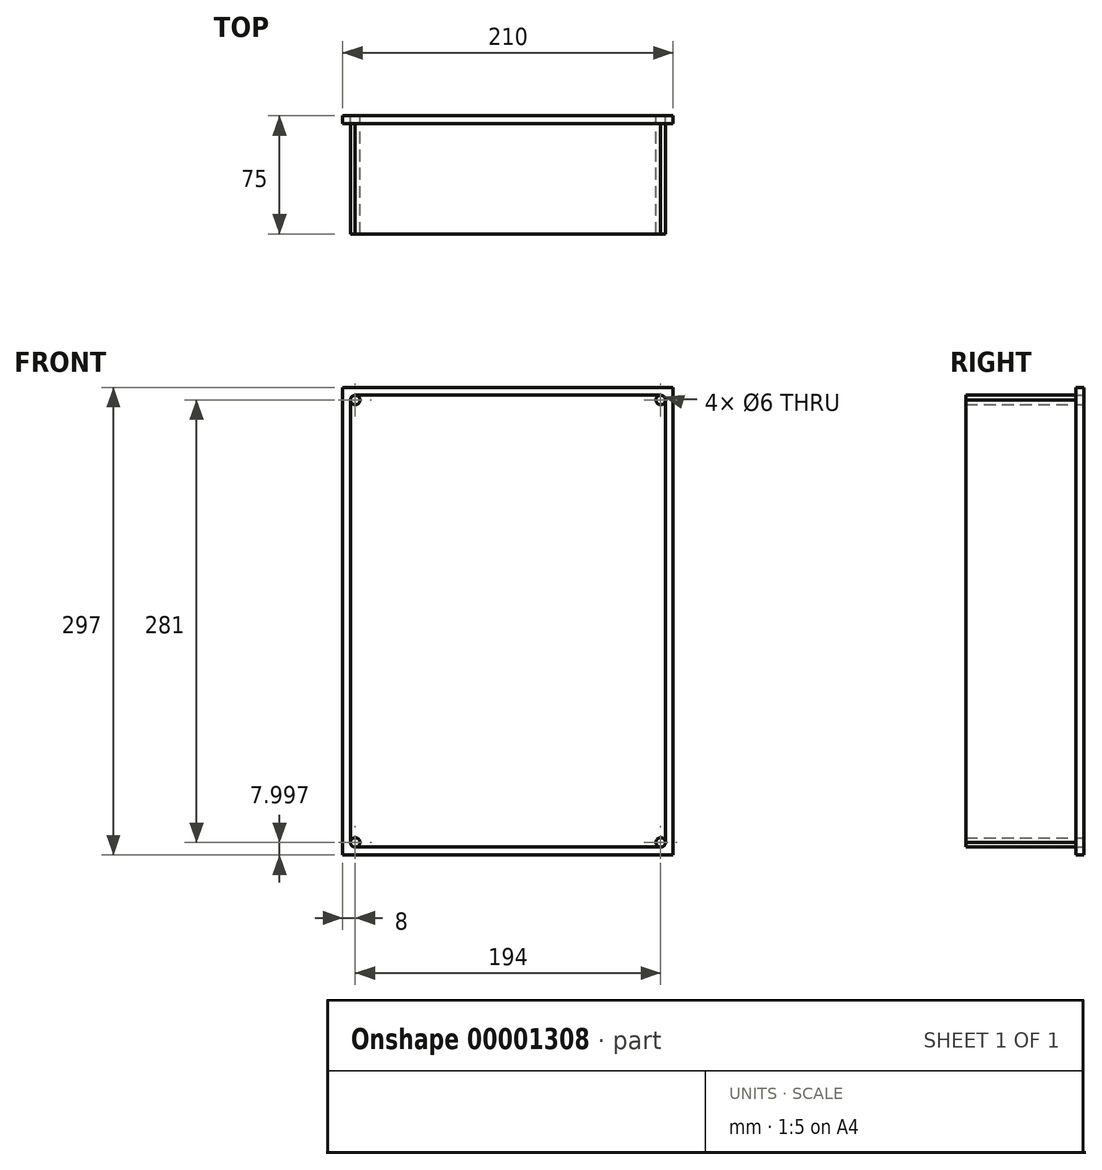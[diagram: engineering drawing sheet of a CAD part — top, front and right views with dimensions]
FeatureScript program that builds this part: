
annotation { "Feature Type Name" : "Feature", "Feature Type Description" : "" }
export const myFeature = defineFeature(function(context is Context, id is Id, definition is map)
    precondition{}
    {
        {
            var Q0;
            Q0=qCreatedBy(makeId("Front.planeOp"),FACE);
            var sketch = newSketch(context, id + "F0", { "sketchPlane" : qUnion([Q0])});
            skLineSegment(sketch, "E0.bottom", {"start": v(0, 297.27) * mm, "end": v(-210, 297.27) * mm});
            skLineSegment(sketch, "E0.top", {"start": v(0, 594.27) * mm, "end": v(-210, 594.27) * mm});
            skLineSegment(sketch, "E0.left", {"start": v(0, 297.27) * mm, "end": v(0, 594.27) * mm});
            skLineSegment(sketch, "E0.right", {"start": v(-210, 297.27) * mm, "end": v(-210, 594.27) * mm});
            skCircle(sketch, "E1", {"center": v(-8, 305.27) * mm, "radius": 3 * mm});
            skCircle(sketch, "E2", {"center": v(-202, 305.27) * mm, "radius": 3 * mm});
            skCircle(sketch, "E3", {"center": v(-8, 586.27) * mm, "radius": 3 * mm});
            skCircle(sketch, "E4", {"center": v(-202, 586.27) * mm, "radius": 3 * mm});
            skSolve(sketch);
        }
        {
            var Q0;
            Q0 = qSketchRegion(id + "F0", true);
            extrude(context, id + "F1", {"entities" : qUnion([Q0]), "depth" : 5 * mm, "offsetDistance" : 25 * mm});
        }
        {
            var Q0;
            Q0=makeQuery(id+"F0.imprint","IMPRINT",FACE,{"disambiguationData":[TD([[makeQuery(id+"F0.imprint","IMPRINT",EDGE,{"derivedFrom":sQuery(id+"F0.wireOp",EDGE,"E0.bottom")}),-1.0]])]});
            extrude(context, id + "F2", {"entities" : qUnion([Q0]), "depth" : 5 * mm, "offsetDistance" : 25 * mm});
        }
        {
            var Q0;
            Q0=makeQuery(id+"F2.opExtrude","SWEPT_EDGE",EDGE,{"disambiguationData":[OSD([sQuery(id+"F0.wireOp",EDGE,"E0.top"),sQuery(id+"F0.wireOp",EDGE,"E0.left")])]});
            var Q1;
            Q1=makeQuery(id+"F2.opExtrude","SWEPT_EDGE",EDGE,{"disambiguationData":[OSD([sQuery(id+"F0.wireOp",EDGE,"E0.bottom"),sQuery(id+"F0.wireOp",EDGE,"E0.left")])]});
            var Q2;
            Q2=makeQuery(id+"F2.opExtrude","SWEPT_EDGE",EDGE,{"disambiguationData":[OSD([sQuery(id+"F0.wireOp",EDGE,"E0.bottom"),sQuery(id+"F0.wireOp",EDGE,"E0.right")])]});
            var Q3;
            Q3=makeQuery(id+"F2.opExtrude","SWEPT_EDGE",EDGE,{"disambiguationData":[OSD([sQuery(id+"F0.wireOp",EDGE,"E0.top"),sQuery(id+"F0.wireOp",EDGE,"E0.right")])]});
            fillet(context, id + "F3", {"entities" : qUnion([Q0, Q1, Q2, Q3]), "radius" : 5 * mm, "tangentPropagation" : true, "allowEdgeOverflow" : false});
        }
        {
            var Q0;
            Q0=makeQuery(id+"F2.opExtrude","CAP_FACE",FACE,{"disambiguationData":[OSD([sQuery(id+"F0.wireOp",EDGE,"E0.bottom"),sQuery(id+"F0.wireOp",EDGE,"E0.top"),sQuery(id+"F0.wireOp",EDGE,"E0.left"),sQuery(id+"F0.wireOp",EDGE,"E0.right"),sQuery(id+"F0.wireOp",EDGE,"E1"),sQuery(id+"F0.wireOp",EDGE,"E2"),sQuery(id+"F0.wireOp",EDGE,"E3"),sQuery(id+"F0.wireOp",EDGE,"E4")])],"isStart":false});
            var sketch = newSketch(context, id + "F4", { "sketchPlane" : qUnion([Q0])});
            skLineSegment(sketch, "E5.bottom", {"start": v(-205, 589.27) * mm, "end": v(-5, 589.27) * mm});
            skLineSegment(sketch, "E5.top", {"start": v(-205, 302.27) * mm, "end": v(-8, 302.27) * mm});
            skLineSegment(sketch, "E5.left", {"start": v(-205, 589.27) * mm, "end": v(-205, 302.27) * mm});
            skLineSegment(sketch, "E5.right", {"start": v(-5, 589.27) * mm, "end": v(-5, 302.27) * mm});
            skSolve(sketch);
        }
        {
            var Q0;
            Q0 = qSketchRegion(id + "F4", true);
            var Q1;
            {var subQ10=makeQuery(id+"F2.opExtrude","CAP_EDGE",EDGE,{"disambiguationData":[OSD([sQuery(id+"F0.wireOp",EDGE,"E4")])],"isStart":false});var subQ13=sQuery(id+"F4.wireOp",EDGE,"E5.bottom");var subQ14=makeQuery(id+"F4.imprint","INTERSECT",VERTEX,{"derivedFrom":[subQ10,subQ13]});Q1=makeQuery(id+"F4.imprint","IMPRINT",FACE,{"disambiguationData":[TD([[makeQuery(id+"F4.imprint","IMPRINT",EDGE,{"disambiguationData":[TD([[subQ14,-1.0]])],"derivedFrom":subQ13}),-1.0]])]});}
            extrude(context, id + "F5", {"entities" : qUnion([Q0, Q1]), "operationType" : NewBodyOperationType.ADD, "depth" : 70 * mm, "offsetDistance" : 25 * mm});
        }
    });
